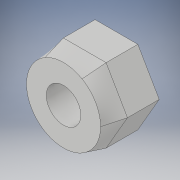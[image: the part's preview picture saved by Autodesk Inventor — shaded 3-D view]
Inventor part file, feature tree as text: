
AUTODESK INVENTOR PART (.ipt)
format: ipt  version: 2018 (Build 220112000, 112)  size: 145,408 bytes
history: native  units: in
note: dims shown in document units (in); Inventor stores cm internally (conversion verified against a paired STEP export)
features: sketch x4, extrude x2, plane x1, loft x1, projected_geometry x1
ambient origin geometry x8: Origin, YZ Plane, XZ Plane, XY Plane, X Axis, Y Axis, Z Axis, Center Point
bodies: Solid1 (feature_tree)
feature tree (9):
  extrude  "Extrusion1"  Depth=0.15in TaperAngle=0.0deg
  sketch  "Sketch2"  dims[d3=0.1in d4=0.35in]
  plane  "Work Plane1"
  loft  "Loft1"
  extrude  "Extrusion2"  TaperAngle=0.0deg  [1 undecoded]
  sketch  "Sketch1"  dims[d0=0.35in d1=0.15in d2=0.0in]
  projected_geometry  "Projected Loop1"
  sketch  "Sketch3"  dims[d5=0.0in d6=90.0deg d7=0.0in d8=90.0deg]
  sketch  "Sketch4"  dims[d9=0.163in d10=1.0in d11=0.0in]
note: 1 required parameter value undecoded (feature->parameter linkage not recoverable at this tier; creation-order binding heuristic only, values carry confidence <= 0.55)
